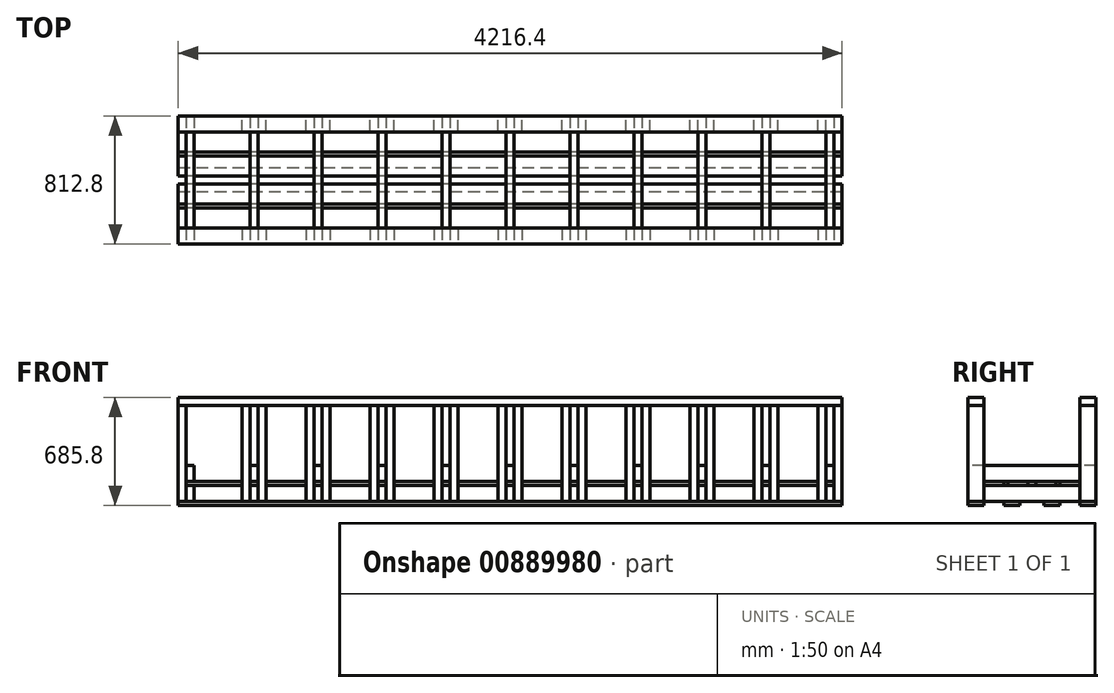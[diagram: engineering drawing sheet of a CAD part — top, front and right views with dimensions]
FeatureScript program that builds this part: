
annotation { "Feature Type Name" : "Feature", "Feature Type Description" : "" }
export const myFeature = defineFeature(function(context is Context, id is Id, definition is map)
    precondition{}
    {
        {
            var Q0;
            Q0=qCreatedBy(makeId("Front.planeOp"),FACE);
            var sketch = newSketch(context, id + "F0", { "sketchPlane" : qUnion([Q0])});
            skLineSegment(sketch, "E0.bottom", {"start": v(-2057.4, 0) * mm, "end": v(-2006.6, 0) * mm});
            skLineSegment(sketch, "E0.top", {"start": v(-2057.4, -101.6) * mm, "end": v(-2006.6, -101.6) * mm});
            skLineSegment(sketch, "E0.left", {"start": v(-2057.4, 0) * mm, "end": v(-2057.4, -101.6) * mm});
            skLineSegment(sketch, "E0.right", {"start": v(-2006.6, 0) * mm, "end": v(-2006.6, -101.6) * mm});
            skLineSegment(sketch, "E1.bottom", {"start": v(-1651, 0) * mm, "end": v(-1600.2, 0) * mm});
            skLineSegment(sketch, "E1.top", {"start": v(-1651, -101.6) * mm, "end": v(-1600.2, -101.6) * mm});
            skLineSegment(sketch, "E1.left", {"start": v(-1651, 0) * mm, "end": v(-1651, -101.6) * mm});
            skLineSegment(sketch, "E1.right", {"start": v(-1600.2, 0) * mm, "end": v(-1600.2, -101.6) * mm});
            skLineSegment(sketch, "E2.bottom", {"start": v(-1244.6, 0) * mm, "end": v(-1193.8, 0) * mm});
            skLineSegment(sketch, "E2.top", {"start": v(-1244.6, -101.6) * mm, "end": v(-1193.8, -101.6) * mm});
            skLineSegment(sketch, "E2.left", {"start": v(-1244.6, 0) * mm, "end": v(-1244.6, -101.6) * mm});
            skLineSegment(sketch, "E2.right", {"start": v(-1193.8, 0) * mm, "end": v(-1193.8, -101.6) * mm});
            skLineSegment(sketch, "E3.bottom", {"start": v(-838.2, 0) * mm, "end": v(-787.4, 0) * mm});
            skLineSegment(sketch, "E3.top", {"start": v(-838.2, -101.6) * mm, "end": v(-787.4, -101.6) * mm});
            skLineSegment(sketch, "E3.left", {"start": v(-838.2, 0) * mm, "end": v(-838.2, -101.6) * mm});
            skLineSegment(sketch, "E3.right", {"start": v(-787.4, 0) * mm, "end": v(-787.4, -101.6) * mm});
            skLineSegment(sketch, "E4.bottom", {"start": v(-431.8, 0) * mm, "end": v(-381, 0) * mm});
            skLineSegment(sketch, "E4.top", {"start": v(-431.8, -101.6) * mm, "end": v(-381, -101.6) * mm});
            skLineSegment(sketch, "E4.left", {"start": v(-431.8, 0) * mm, "end": v(-431.8, -101.6) * mm});
            skLineSegment(sketch, "E4.right", {"start": v(-381, 0) * mm, "end": v(-381, -101.6) * mm});
            skLineSegment(sketch, "E5.bottom", {"start": v(-25.4, 0) * mm, "end": v(25.4, 0) * mm});
            skLineSegment(sketch, "E5.top", {"start": v(-25.4, -101.6) * mm, "end": v(25.4, -101.6) * mm});
            skLineSegment(sketch, "E5.left", {"start": v(-25.4, 0) * mm, "end": v(-25.4, -101.6) * mm});
            skLineSegment(sketch, "E5.right", {"start": v(25.4, 0) * mm, "end": v(25.4, -101.6) * mm});
            skLineSegment(sketch, "E6", {"start": v(0, 664.62) * mm, "end": v(0, -825.58) * mm, "construction": true});
            skPoint(sketch, "E7", {"position": v(-2108.2, -101.6) * mm});
            skPoint(sketch, "E8", {"position": v(-2032, 0) * mm});
            skPoint(sketch, "E9", {"position": v(-1625.6, 0) * mm});
            skPoint(sketch, "E10", {"position": v(-1219.2, 0) * mm});
            skPoint(sketch, "E11", {"position": v(-812.8, 0) * mm});
            skPoint(sketch, "E12", {"position": v(-406.4, 0) * mm});
            skLineSegment(sketch, "E13.MirrorCS", {"start": v(2057.4, 0) * mm, "end": v(2006.6, 0) * mm});
            skLineSegment(sketch, "E14.MirrorCS", {"start": v(2057.4, -101.6) * mm, "end": v(2006.6, -101.6) * mm});
            skLineSegment(sketch, "E15.MirrorCS", {"start": v(1651, -101.6) * mm, "end": v(1600.2, -101.6) * mm});
            skLineSegment(sketch, "E16.MirrorCS", {"start": v(838.2, -101.6) * mm, "end": v(787.4, -101.6) * mm});
            skLineSegment(sketch, "E17.MirrorCS", {"start": v(1244.6, 0) * mm, "end": v(1193.8, 0) * mm});
            skLineSegment(sketch, "E18.MirrorCS", {"start": v(1651, 0) * mm, "end": v(1600.2, 0) * mm});
            skLineSegment(sketch, "E19.MirrorCS", {"start": v(431.8, 0) * mm, "end": v(381, 0) * mm});
            skLineSegment(sketch, "E20.MirrorCS", {"start": v(431.8, -101.6) * mm, "end": v(381, -101.6) * mm});
            skLineSegment(sketch, "E21.MirrorCS", {"start": v(1244.6, -101.6) * mm, "end": v(1193.8, -101.6) * mm});
            skLineSegment(sketch, "E22.MirrorCS", {"start": v(838.2, 0) * mm, "end": v(787.4, 0) * mm});
            skPoint(sketch, "E23.MirrorP", {"position": v(1625.6, 0) * mm});
            skLineSegment(sketch, "E24.MirrorCS", {"start": v(1193.8, 0) * mm, "end": v(1193.8, -101.6) * mm});
            skLineSegment(sketch, "E25.MirrorCS", {"start": v(838.2, 0) * mm, "end": v(838.2, -101.6) * mm});
            skLineSegment(sketch, "E26.MirrorCS", {"start": v(1244.6, 0) * mm, "end": v(1244.6, -101.6) * mm});
            skPoint(sketch, "E27.MirrorP", {"position": v(406.4, 0) * mm});
            skPoint(sketch, "E28.MirrorP", {"position": v(1219.2, 0) * mm});
            skLineSegment(sketch, "E29.MirrorCS", {"start": v(1600.2, 0) * mm, "end": v(1600.2, -101.6) * mm});
            skLineSegment(sketch, "E30.MirrorCS", {"start": v(1651, 0) * mm, "end": v(1651, -101.6) * mm});
            skLineSegment(sketch, "E31.MirrorCS", {"start": v(2057.4, 0) * mm, "end": v(2057.4, -101.6) * mm});
            skLineSegment(sketch, "E32.MirrorCS", {"start": v(2006.6, 0) * mm, "end": v(2006.6, -101.6) * mm});
            skPoint(sketch, "E33.MirrorP", {"position": v(812.8, 0) * mm});
            skLineSegment(sketch, "E34.MirrorCS", {"start": v(787.4, 0) * mm, "end": v(787.4, -101.6) * mm});
            skLineSegment(sketch, "E35.MirrorCS", {"start": v(381, 0) * mm, "end": v(381, -101.6) * mm});
            skPoint(sketch, "E36.MirrorP", {"position": v(2108.2, -101.6) * mm});
            skPoint(sketch, "E37.MirrorP", {"position": v(2032, 0) * mm});
            skLineSegment(sketch, "E38.MirrorCS", {"start": v(431.8, 0) * mm, "end": v(431.8, -101.6) * mm});
            skSolve(sketch);
        }
        {
            var Q0;
            Q0=qSketchRegion(id+"F0",true);
            extrude(context, id + "F1", {"entities" : qUnion([Q0]), "endBound" : BoundingType.SYMMETRIC, "oppositeDirection" : true, "depth" : 812.8 * mm, "offsetDistance" : 25.4 * mm});
        }
        {
            var Q0;
            Q0=makeQuery(id+"F1.opExtrude","SWEPT_FACE",FACE,{"disambiguationData":[OSD([sQuery(id+"F0.wireOp",EDGE,"E0.left")])]});
            var sketch = newSketch(context, id + "F2", { "sketchPlane" : qUnion([Q0])});
            skLineSegment(sketch, "E39.bottom", {"start": v(-25.4, 0) * mm, "end": v(-152.4, 0) * mm});
            skLineSegment(sketch, "E39.top", {"start": v(-25.4, 25.4) * mm, "end": v(-152.4, 25.4) * mm});
            skLineSegment(sketch, "E39.left", {"start": v(-25.4, 0) * mm, "end": v(-25.4, 25.4) * mm});
            skLineSegment(sketch, "E39.right", {"start": v(-152.4, 0) * mm, "end": v(-152.4, 25.4) * mm});
            skLineSegment(sketch, "E40", {"start": v(0, 367.43) * mm, "end": v(0, -336.71) * mm, "construction": true});
            skPoint(sketch, "E40.endSnap0", {"position": v(0, -101.6) * mm});
            skLineSegment(sketch, "E41.bottom", {"start": v(-304.8, 0) * mm, "end": v(-177.8, 0) * mm});
            skLineSegment(sketch, "E41.top", {"start": v(-304.8, 25.4) * mm, "end": v(-177.8, 25.4) * mm});
            skLineSegment(sketch, "E41.left", {"start": v(-304.8, 0) * mm, "end": v(-304.8, 25.4) * mm});
            skLineSegment(sketch, "E41.right", {"start": v(-177.8, 0) * mm, "end": v(-177.8, 25.4) * mm});
            skLineSegment(sketch, "E42.bottom", {"start": v(-406.4, -101.6) * mm, "end": v(-304.8, -101.6) * mm});
            skLineSegment(sketch, "E42.top", {"start": v(-406.4, -127) * mm, "end": v(-304.8, -127) * mm});
            skLineSegment(sketch, "E42.left", {"start": v(-406.4, -101.6) * mm, "end": v(-406.4, -127) * mm});
            skLineSegment(sketch, "E42.right", {"start": v(-304.8, -101.6) * mm, "end": v(-304.8, -127) * mm});
            skLineSegment(sketch, "E43.MirrorCS", {"start": v(152.4, 0) * mm, "end": v(152.4, 25.4) * mm});
            skLineSegment(sketch, "E44.MirrorCS", {"start": v(304.8, 0) * mm, "end": v(177.8, 0) * mm});
            skLineSegment(sketch, "E45.MirrorCS", {"start": v(304.8, 25.4) * mm, "end": v(177.8, 25.4) * mm});
            skLineSegment(sketch, "E46.MirrorCS", {"start": v(25.4, 0) * mm, "end": v(152.4, 0) * mm});
            skLineSegment(sketch, "E47.MirrorCS", {"start": v(177.8, 0) * mm, "end": v(177.8, 25.4) * mm});
            skLineSegment(sketch, "E48.MirrorCS", {"start": v(406.4, -101.6) * mm, "end": v(406.4, -127) * mm});
            skLineSegment(sketch, "E49.MirrorCS", {"start": v(25.4, 25.4) * mm, "end": v(152.4, 25.4) * mm});
            skLineSegment(sketch, "E50.MirrorCS", {"start": v(304.8, 0) * mm, "end": v(304.8, 25.4) * mm});
            skLineSegment(sketch, "E51.MirrorCS", {"start": v(406.4, -127) * mm, "end": v(304.8, -127) * mm});
            skLineSegment(sketch, "E52.MirrorCS", {"start": v(304.8, -101.6) * mm, "end": v(304.8, -127) * mm});
            skLineSegment(sketch, "E53.MirrorCS", {"start": v(406.4, -101.6) * mm, "end": v(304.8, -101.6) * mm});
            skLineSegment(sketch, "E54.MirrorCS", {"start": v(25.4, 0) * mm, "end": v(25.4, 25.4) * mm});
            skLineSegment(sketch, "E55.bottom", {"start": v(-177.8, -101.6) * mm, "end": v(-76.2, -101.6) * mm});
            skLineSegment(sketch, "E55.top", {"start": v(-177.8, -127) * mm, "end": v(-76.2, -127) * mm});
            skLineSegment(sketch, "E55.left", {"start": v(-177.8, -101.6) * mm, "end": v(-177.8, -127) * mm});
            skLineSegment(sketch, "E55.right", {"start": v(-76.2, -101.6) * mm, "end": v(-76.2, -127) * mm});
            skLineSegment(sketch, "E56.MirrorCS", {"start": v(177.8, -101.6) * mm, "end": v(76.2, -101.6) * mm});
            skLineSegment(sketch, "E57.MirrorCS", {"start": v(76.2, -101.6) * mm, "end": v(76.2, -127) * mm});
            skLineSegment(sketch, "E58.MirrorCS", {"start": v(177.8, -101.6) * mm, "end": v(177.8, -127) * mm});
            skLineSegment(sketch, "E59.MirrorCS", {"start": v(177.8, -127) * mm, "end": v(76.2, -127) * mm});
            skSolve(sketch);
        }
        {
            var Q0;
            Q0=qSketchRegion(id+"F2",true);
            var Q1;
            Q1=makeQuery(id+"F1.opExtrude","SWEPT_FACE",FACE,{"disambiguationData":[OSD([sQuery(id+"F0.wireOp",EDGE,"E31.MirrorCS")])]});
            extrude(context, id + "F3", {"entities" : qUnion([Q0]), "endBound" : BoundingType.UP_TO_SURFACE, "oppositeDirection" : true, "depth" : 25.4 * mm, "endBoundEntityFace" : qUnion([Q1]), "hasOffset" : true, "offsetDistance" : -50.8 * mm, "hasSecondDirection" : true, "secondDirectionOppositeDirection" : false, "secondDirectionDepth" : 50.8 * mm});
        }
        {
            var Q0;
            Q0=makeQuery(id+"F3.opExtrude","SWEPT_FACE",FACE,{"disambiguationData":[OSD([sQuery(id+"F2.wireOp",EDGE,"E48.MirrorCS")])]});
            var sketch = newSketch(context, id + "F4", { "sketchPlane" : qUnion([Q0])});
            skLineSegment(sketch, "E60.0", {"start": v(-2057.4, 0) * mm, "end": v(-2057.4, -101.6) * mm});
            skLineSegment(sketch, "E61.0", {"start": v(-2006.6, 0) * mm, "end": v(-2006.6, -101.6) * mm});
            skLineSegment(sketch, "E62.0", {"start": v(-1651, 0) * mm, "end": v(-1651, -101.6) * mm});
            skLineSegment(sketch, "E63.0", {"start": v(-1600.2, 0) * mm, "end": v(-1600.2, -101.6) * mm});
            skLineSegment(sketch, "E64.0", {"start": v(-1244.6, 0) * mm, "end": v(-1244.6, -101.6) * mm});
            skLineSegment(sketch, "E65.0", {"start": v(-1193.8, 0) * mm, "end": v(-1193.8, -101.6) * mm});
            skLineSegment(sketch, "E66.0", {"start": v(-838.2, 0) * mm, "end": v(-838.2, -101.6) * mm});
            skLineSegment(sketch, "E67.0", {"start": v(-787.4, 0) * mm, "end": v(-787.4, -101.6) * mm});
            skLineSegment(sketch, "E68.0", {"start": v(-431.8, 0) * mm, "end": v(-431.8, -101.6) * mm});
            skLineSegment(sketch, "E69.0", {"start": v(-381, 0) * mm, "end": v(-381, -101.6) * mm});
            skLineSegment(sketch, "E70.0", {"start": v(-25.4, 0) * mm, "end": v(-25.4, -101.6) * mm});
            skLineSegment(sketch, "E71.0", {"start": v(25.4, 0) * mm, "end": v(25.4, -101.6) * mm});
            skLineSegment(sketch, "E72.0", {"start": v(381, 0) * mm, "end": v(381, -101.6) * mm});
            skLineSegment(sketch, "E73.0", {"start": v(431.8, 0) * mm, "end": v(431.8, -101.6) * mm});
            skLineSegment(sketch, "E74.0", {"start": v(787.4, 0) * mm, "end": v(787.4, -101.6) * mm});
            skLineSegment(sketch, "E75.0", {"start": v(838.2, 0) * mm, "end": v(838.2, -101.6) * mm});
            skLineSegment(sketch, "E76.0", {"start": v(1193.8, 0) * mm, "end": v(1193.8, -101.6) * mm});
            skLineSegment(sketch, "E77.0", {"start": v(1244.6, 0) * mm, "end": v(1244.6, -101.6) * mm});
            skLineSegment(sketch, "E78.0", {"start": v(1600.2, 0) * mm, "end": v(1600.2, -101.6) * mm});
            skLineSegment(sketch, "E79.0", {"start": v(1651, 0) * mm, "end": v(1651, -101.6) * mm});
            skLineSegment(sketch, "E80.0", {"start": v(2006.6, 0) * mm, "end": v(2006.6, -101.6) * mm});
            skLineSegment(sketch, "E81.0", {"start": v(2057.4, 0) * mm, "end": v(2057.4, -101.6) * mm});
            skLineSegment(sketch, "E82.bottom", {"start": v(-2057.4, 25.4) * mm, "end": v(-2006.6, 25.4) * mm});
            skLineSegment(sketch, "E82.top", {"start": v(-2057.4, 127) * mm, "end": v(-2006.6, 127) * mm});
            skLineSegment(sketch, "E82.left", {"start": v(-2057.4, 25.4) * mm, "end": v(-2057.4, 127) * mm});
            skLineSegment(sketch, "E82.right", {"start": v(-2006.6, 25.4) * mm, "end": v(-2006.6, 127) * mm});
            skLineSegment(sketch, "E83.bottom", {"start": v(-1651, 25.4) * mm, "end": v(-1600.2, 25.4) * mm});
            skLineSegment(sketch, "E83.top", {"start": v(-1651, 127) * mm, "end": v(-1600.2, 127) * mm});
            skLineSegment(sketch, "E83.left", {"start": v(-1651, 25.4) * mm, "end": v(-1651, 127) * mm});
            skLineSegment(sketch, "E83.right", {"start": v(-1600.2, 25.4) * mm, "end": v(-1600.2, 127) * mm});
            skLineSegment(sketch, "E84.bottom", {"start": v(-1244.6, 25.4) * mm, "end": v(-1193.8, 25.4) * mm});
            skLineSegment(sketch, "E84.top", {"start": v(-1244.6, 127) * mm, "end": v(-1193.8, 127) * mm});
            skLineSegment(sketch, "E84.left", {"start": v(-1244.6, 25.4) * mm, "end": v(-1244.6, 127) * mm});
            skLineSegment(sketch, "E84.right", {"start": v(-1193.8, 25.4) * mm, "end": v(-1193.8, 127) * mm});
            skLineSegment(sketch, "E85.bottom", {"start": v(-838.2, 25.4) * mm, "end": v(-787.4, 25.4) * mm});
            skLineSegment(sketch, "E85.top", {"start": v(-838.2, 127) * mm, "end": v(-787.4, 127) * mm});
            skLineSegment(sketch, "E85.left", {"start": v(-838.2, 25.4) * mm, "end": v(-838.2, 127) * mm});
            skLineSegment(sketch, "E85.right", {"start": v(-787.4, 25.4) * mm, "end": v(-787.4, 127) * mm});
            skLineSegment(sketch, "E86.bottom", {"start": v(-431.8, 25.4) * mm, "end": v(-381, 25.4) * mm});
            skLineSegment(sketch, "E86.top", {"start": v(-431.8, 127) * mm, "end": v(-381, 127) * mm});
            skLineSegment(sketch, "E86.left", {"start": v(-431.8, 25.4) * mm, "end": v(-431.8, 127) * mm});
            skLineSegment(sketch, "E86.right", {"start": v(-381, 25.4) * mm, "end": v(-381, 127) * mm});
            skLineSegment(sketch, "E87.bottom", {"start": v(-25.4, 25.4) * mm, "end": v(25.4, 25.4) * mm});
            skLineSegment(sketch, "E87.top", {"start": v(-25.4, 127) * mm, "end": v(25.4, 127) * mm});
            skLineSegment(sketch, "E87.left", {"start": v(-25.4, 25.4) * mm, "end": v(-25.4, 127) * mm});
            skLineSegment(sketch, "E87.right", {"start": v(25.4, 25.4) * mm, "end": v(25.4, 127) * mm});
            skLineSegment(sketch, "E88.bottom", {"start": v(381, 25.4) * mm, "end": v(431.8, 25.4) * mm});
            skLineSegment(sketch, "E88.top", {"start": v(381, 127) * mm, "end": v(431.8, 127) * mm});
            skLineSegment(sketch, "E88.left", {"start": v(381, 25.4) * mm, "end": v(381, 127) * mm});
            skLineSegment(sketch, "E88.right", {"start": v(431.8, 25.4) * mm, "end": v(431.8, 127) * mm});
            skLineSegment(sketch, "E89.bottom", {"start": v(787.4, 25.4) * mm, "end": v(838.2, 25.4) * mm});
            skLineSegment(sketch, "E89.top", {"start": v(787.4, 127) * mm, "end": v(838.2, 127) * mm});
            skLineSegment(sketch, "E89.left", {"start": v(787.4, 25.4) * mm, "end": v(787.4, 127) * mm});
            skLineSegment(sketch, "E89.right", {"start": v(838.2, 25.4) * mm, "end": v(838.2, 127) * mm});
            skLineSegment(sketch, "E90.bottom", {"start": v(1193.8, 25.4) * mm, "end": v(1244.6, 25.4) * mm});
            skLineSegment(sketch, "E90.top", {"start": v(1193.8, 127) * mm, "end": v(1244.6, 127) * mm});
            skLineSegment(sketch, "E90.left", {"start": v(1193.8, 25.4) * mm, "end": v(1193.8, 127) * mm});
            skLineSegment(sketch, "E90.right", {"start": v(1244.6, 25.4) * mm, "end": v(1244.6, 127) * mm});
            skLineSegment(sketch, "E91.bottom", {"start": v(1600.2, 25.4) * mm, "end": v(1651, 25.4) * mm});
            skLineSegment(sketch, "E91.top", {"start": v(1600.2, 127) * mm, "end": v(1651, 127) * mm});
            skLineSegment(sketch, "E91.left", {"start": v(1600.2, 25.4) * mm, "end": v(1600.2, 127) * mm});
            skLineSegment(sketch, "E91.right", {"start": v(1651, 25.4) * mm, "end": v(1651, 127) * mm});
            skLineSegment(sketch, "E92.bottom", {"start": v(2006.6, 25.4) * mm, "end": v(2057.4, 25.4) * mm});
            skLineSegment(sketch, "E92.top", {"start": v(2006.6, 127) * mm, "end": v(2057.4, 127) * mm});
            skLineSegment(sketch, "E92.left", {"start": v(2006.6, 25.4) * mm, "end": v(2006.6, 127) * mm});
            skLineSegment(sketch, "E92.right", {"start": v(2057.4, 25.4) * mm, "end": v(2057.4, 127) * mm});
            skSolve(sketch);
        }
        {
            var Q0;
            Q0=qSketchRegion(id+"F4",true);
            var Q1;
            Q1=makeQuery(id+"F1.opExtrude","CAP_FACE",FACE,{"disambiguationData":[OSD([sQuery(id+"F0.wireOp",EDGE,"E0.bottom"),sQuery(id+"F0.wireOp",EDGE,"E0.top"),sQuery(id+"F0.wireOp",EDGE,"E0.left"),sQuery(id+"F0.wireOp",EDGE,"E0.right")])],"isStart":false});
            extrude(context, id + "F5", {"entities" : qUnion([Q0]), "endBound" : BoundingType.UP_TO_SURFACE, "oppositeDirection" : true, "depth" : 25.4 * mm, "endBoundEntityFace" : qUnion([Q1]), "offsetDistance" : 25.4 * mm});
        }
        {
            var Q0;
            Q0=makeQuery(id+"F3.opExtrude","SWEPT_FACE",FACE,{"disambiguationData":[OSD([sQuery(id+"F2.wireOp",EDGE,"E48.MirrorCS")])]});
            var sketch = newSketch(context, id + "F6", { "sketchPlane" : qUnion([Q0])});
            skLineSegment(sketch, "E93.0", {"start": v(-2057.4, 0) * mm, "end": v(-2057.4, -101.6) * mm});
            skLineSegment(sketch, "E94.0", {"start": v(-2006.6, 0) * mm, "end": v(-2006.6, -101.6) * mm});
            skLineSegment(sketch, "E95.0", {"start": v(-1651, 0) * mm, "end": v(-1651, -101.6) * mm});
            skLineSegment(sketch, "E96.0", {"start": v(-1600.2, 0) * mm, "end": v(-1600.2, -101.6) * mm});
            skLineSegment(sketch, "E97.0", {"start": v(-1193.8, 0) * mm, "end": v(-1193.8, -101.6) * mm});
            skLineSegment(sketch, "E98.0", {"start": v(-1244.6, 0) * mm, "end": v(-1244.6, -101.6) * mm});
            skLineSegment(sketch, "E99.0", {"start": v(-838.2, 0) * mm, "end": v(-838.2, -101.6) * mm});
            skLineSegment(sketch, "E100.0", {"start": v(-787.4, 0) * mm, "end": v(-787.4, -101.6) * mm});
            skLineSegment(sketch, "E101.0", {"start": v(-431.8, 0) * mm, "end": v(-431.8, -101.6) * mm});
            skLineSegment(sketch, "E102.0", {"start": v(-381, 0) * mm, "end": v(-381, -101.6) * mm});
            skLineSegment(sketch, "E103.0", {"start": v(-25.4, 0) * mm, "end": v(-25.4, -101.6) * mm});
            skLineSegment(sketch, "E104.0", {"start": v(25.4, 0) * mm, "end": v(25.4, -101.6) * mm});
            skLineSegment(sketch, "E105.0", {"start": v(381, 0) * mm, "end": v(381, -101.6) * mm});
            skLineSegment(sketch, "E106.0", {"start": v(431.8, 0) * mm, "end": v(431.8, -101.6) * mm});
            skLineSegment(sketch, "E107.0", {"start": v(787.4, 0) * mm, "end": v(787.4, -101.6) * mm});
            skLineSegment(sketch, "E108.0", {"start": v(838.2, 0) * mm, "end": v(838.2, -101.6) * mm});
            skLineSegment(sketch, "E109.0", {"start": v(1193.8, 0) * mm, "end": v(1193.8, -101.6) * mm});
            skLineSegment(sketch, "E110.0", {"start": v(1244.6, 0) * mm, "end": v(1244.6, -101.6) * mm});
            skLineSegment(sketch, "E111.0", {"start": v(1600.2, 0) * mm, "end": v(1600.2, -101.6) * mm});
            skLineSegment(sketch, "E112.0", {"start": v(1651, 0) * mm, "end": v(1651, -101.6) * mm});
            skLineSegment(sketch, "E113.0", {"start": v(2006.6, 0) * mm, "end": v(2006.6, -101.6) * mm});
            skLineSegment(sketch, "E114.0", {"start": v(2057.4, 0) * mm, "end": v(2057.4, -101.6) * mm});
            skLineSegment(sketch, "E115.bottom", {"start": v(-2108.2, -101.6) * mm, "end": v(-2057.4, -101.6) * mm});
            skLineSegment(sketch, "E115.top", {"start": v(-2108.2, 508) * mm, "end": v(-2057.4, 508) * mm});
            skLineSegment(sketch, "E115.left", {"start": v(-2108.2, -101.6) * mm, "end": v(-2108.2, 508) * mm});
            skLineSegment(sketch, "E115.right", {"start": v(-2057.4, -101.6) * mm, "end": v(-2057.4, 508) * mm});
            skLineSegment(sketch, "E116.bottom", {"start": v(-1651, -101.6) * mm, "end": v(-1701.8, -101.6) * mm});
            skLineSegment(sketch, "E116.top", {"start": v(-1651, 508) * mm, "end": v(-1701.8, 508) * mm});
            skLineSegment(sketch, "E116.left", {"start": v(-1651, -101.6) * mm, "end": v(-1651, 508) * mm});
            skLineSegment(sketch, "E116.right", {"start": v(-1701.8, -101.6) * mm, "end": v(-1701.8, 508) * mm});
            skLineSegment(sketch, "E117.bottom", {"start": v(-1600.2, -101.6) * mm, "end": v(-1549.4, -101.6) * mm});
            skLineSegment(sketch, "E117.top", {"start": v(-1600.2, 508) * mm, "end": v(-1549.4, 508) * mm});
            skLineSegment(sketch, "E117.left", {"start": v(-1600.2, -101.6) * mm, "end": v(-1600.2, 508) * mm});
            skLineSegment(sketch, "E117.right", {"start": v(-1549.4, -101.6) * mm, "end": v(-1549.4, 508) * mm});
            skLineSegment(sketch, "E118.bottom", {"start": v(-1244.6, -101.6) * mm, "end": v(-1295.4, -101.6) * mm});
            skLineSegment(sketch, "E118.top", {"start": v(-1244.6, 508) * mm, "end": v(-1295.4, 508) * mm});
            skLineSegment(sketch, "E118.left", {"start": v(-1244.6, -101.6) * mm, "end": v(-1244.6, 508) * mm});
            skLineSegment(sketch, "E118.right", {"start": v(-1295.4, -101.6) * mm, "end": v(-1295.4, 508) * mm});
            skLineSegment(sketch, "E119.bottom", {"start": v(-1193.8, -101.6) * mm, "end": v(-1143, -101.6) * mm});
            skLineSegment(sketch, "E119.top", {"start": v(-1193.8, 508) * mm, "end": v(-1143, 508) * mm});
            skLineSegment(sketch, "E119.left", {"start": v(-1193.8, -101.6) * mm, "end": v(-1193.8, 508) * mm});
            skLineSegment(sketch, "E119.right", {"start": v(-1143, -101.6) * mm, "end": v(-1143, 508) * mm});
            skLineSegment(sketch, "E120.bottom", {"start": v(-838.2, -101.6) * mm, "end": v(-889, -101.6) * mm});
            skLineSegment(sketch, "E120.top", {"start": v(-838.2, 508) * mm, "end": v(-889, 508) * mm});
            skLineSegment(sketch, "E120.left", {"start": v(-838.2, -101.6) * mm, "end": v(-838.2, 508) * mm});
            skLineSegment(sketch, "E120.right", {"start": v(-889, -101.6) * mm, "end": v(-889, 508) * mm});
            skLineSegment(sketch, "E121.bottom", {"start": v(-787.4, -101.6) * mm, "end": v(-736.6, -101.6) * mm});
            skLineSegment(sketch, "E121.top", {"start": v(-787.4, 508) * mm, "end": v(-736.6, 508) * mm});
            skLineSegment(sketch, "E121.left", {"start": v(-787.4, -101.6) * mm, "end": v(-787.4, 508) * mm});
            skLineSegment(sketch, "E121.right", {"start": v(-736.6, -101.6) * mm, "end": v(-736.6, 508) * mm});
            skLineSegment(sketch, "E122.bottom", {"start": v(-431.8, -101.6) * mm, "end": v(-482.6, -101.6) * mm});
            skLineSegment(sketch, "E122.top", {"start": v(-431.8, 508) * mm, "end": v(-482.6, 508) * mm});
            skLineSegment(sketch, "E122.left", {"start": v(-431.8, -101.6) * mm, "end": v(-431.8, 508) * mm});
            skLineSegment(sketch, "E122.right", {"start": v(-482.6, -101.6) * mm, "end": v(-482.6, 508) * mm});
            skLineSegment(sketch, "E123.bottom", {"start": v(-381, -101.6) * mm, "end": v(-330.2, -101.6) * mm});
            skLineSegment(sketch, "E123.top", {"start": v(-381, 508) * mm, "end": v(-330.2, 508) * mm});
            skLineSegment(sketch, "E123.left", {"start": v(-381, -101.6) * mm, "end": v(-381, 508) * mm});
            skLineSegment(sketch, "E123.right", {"start": v(-330.2, -101.6) * mm, "end": v(-330.2, 508) * mm});
            skLineSegment(sketch, "E124.bottom", {"start": v(-25.4, -101.6) * mm, "end": v(-76.2, -101.6) * mm});
            skLineSegment(sketch, "E124.top", {"start": v(-25.4, 508) * mm, "end": v(-76.2, 508) * mm});
            skLineSegment(sketch, "E124.left", {"start": v(-25.4, -101.6) * mm, "end": v(-25.4, 508) * mm});
            skLineSegment(sketch, "E124.right", {"start": v(-76.2, -101.6) * mm, "end": v(-76.2, 508) * mm});
            skLineSegment(sketch, "E125.bottom", {"start": v(25.4, -101.6) * mm, "end": v(76.2, -101.6) * mm});
            skLineSegment(sketch, "E125.top", {"start": v(25.4, 508) * mm, "end": v(76.2, 508) * mm});
            skLineSegment(sketch, "E125.left", {"start": v(25.4, -101.6) * mm, "end": v(25.4, 508) * mm});
            skLineSegment(sketch, "E125.right", {"start": v(76.2, -101.6) * mm, "end": v(76.2, 508) * mm});
            skLineSegment(sketch, "E126.bottom", {"start": v(381, -101.6) * mm, "end": v(330.2, -101.6) * mm});
            skLineSegment(sketch, "E126.top", {"start": v(381, 508) * mm, "end": v(330.2, 508) * mm});
            skLineSegment(sketch, "E126.left", {"start": v(381, -101.6) * mm, "end": v(381, 508) * mm});
            skLineSegment(sketch, "E126.right", {"start": v(330.2, -101.6) * mm, "end": v(330.2, 508) * mm});
            skLineSegment(sketch, "E127.bottom", {"start": v(431.8, -101.6) * mm, "end": v(482.6, -101.6) * mm});
            skLineSegment(sketch, "E127.top", {"start": v(431.8, 508) * mm, "end": v(482.6, 508) * mm});
            skLineSegment(sketch, "E127.left", {"start": v(431.8, -101.6) * mm, "end": v(431.8, 508) * mm});
            skLineSegment(sketch, "E127.right", {"start": v(482.6, -101.6) * mm, "end": v(482.6, 508) * mm});
            skLineSegment(sketch, "E128.bottom", {"start": v(787.4, -101.6) * mm, "end": v(736.6, -101.6) * mm});
            skLineSegment(sketch, "E128.top", {"start": v(787.4, 508) * mm, "end": v(736.6, 508) * mm});
            skLineSegment(sketch, "E128.left", {"start": v(787.4, -101.6) * mm, "end": v(787.4, 508) * mm});
            skLineSegment(sketch, "E128.right", {"start": v(736.6, -101.6) * mm, "end": v(736.6, 508) * mm});
            skLineSegment(sketch, "E129.bottom", {"start": v(838.2, -101.6) * mm, "end": v(889, -101.6) * mm});
            skLineSegment(sketch, "E129.top", {"start": v(838.2, 508) * mm, "end": v(889, 508) * mm});
            skLineSegment(sketch, "E129.left", {"start": v(838.2, -101.6) * mm, "end": v(838.2, 508) * mm});
            skLineSegment(sketch, "E129.right", {"start": v(889, -101.6) * mm, "end": v(889, 508) * mm});
            skLineSegment(sketch, "E130.bottom", {"start": v(1193.8, -101.6) * mm, "end": v(1143, -101.6) * mm});
            skLineSegment(sketch, "E130.top", {"start": v(1193.8, 508) * mm, "end": v(1143, 508) * mm});
            skLineSegment(sketch, "E130.left", {"start": v(1193.8, -101.6) * mm, "end": v(1193.8, 508) * mm});
            skLineSegment(sketch, "E130.right", {"start": v(1143, -101.6) * mm, "end": v(1143, 508) * mm});
            skLineSegment(sketch, "E131.bottom", {"start": v(1244.6, -101.6) * mm, "end": v(1295.4, -101.6) * mm});
            skLineSegment(sketch, "E131.top", {"start": v(1244.6, 508) * mm, "end": v(1295.4, 508) * mm});
            skLineSegment(sketch, "E131.left", {"start": v(1244.6, -101.6) * mm, "end": v(1244.6, 508) * mm});
            skLineSegment(sketch, "E131.right", {"start": v(1295.4, -101.6) * mm, "end": v(1295.4, 508) * mm});
            skLineSegment(sketch, "E132.bottom", {"start": v(1600.2, -101.6) * mm, "end": v(1549.4, -101.6) * mm});
            skLineSegment(sketch, "E132.top", {"start": v(1600.2, 508) * mm, "end": v(1549.4, 508) * mm});
            skLineSegment(sketch, "E132.left", {"start": v(1600.2, -101.6) * mm, "end": v(1600.2, 508) * mm});
            skLineSegment(sketch, "E132.right", {"start": v(1549.4, -101.6) * mm, "end": v(1549.4, 508) * mm});
            skLineSegment(sketch, "E133.bottom", {"start": v(1651, -101.6) * mm, "end": v(1701.8, -101.6) * mm});
            skLineSegment(sketch, "E133.top", {"start": v(1651, 508) * mm, "end": v(1701.8, 508) * mm});
            skLineSegment(sketch, "E133.left", {"start": v(1651, -101.6) * mm, "end": v(1651, 508) * mm});
            skLineSegment(sketch, "E133.right", {"start": v(1701.8, -101.6) * mm, "end": v(1701.8, 508) * mm});
            skLineSegment(sketch, "E134.bottom", {"start": v(2006.6, -101.6) * mm, "end": v(1955.8, -101.6) * mm});
            skLineSegment(sketch, "E134.top", {"start": v(2006.6, 508) * mm, "end": v(1955.8, 508) * mm});
            skLineSegment(sketch, "E134.left", {"start": v(2006.6, -101.6) * mm, "end": v(2006.6, 508) * mm});
            skLineSegment(sketch, "E134.right", {"start": v(1955.8, -101.6) * mm, "end": v(1955.8, 508) * mm});
            skLineSegment(sketch, "E135.bottom", {"start": v(2057.4, -101.6) * mm, "end": v(2108.2, -101.6) * mm});
            skLineSegment(sketch, "E135.top", {"start": v(2057.4, 508) * mm, "end": v(2108.2, 508) * mm});
            skLineSegment(sketch, "E135.left", {"start": v(2057.4, -101.6) * mm, "end": v(2057.4, 508) * mm});
            skLineSegment(sketch, "E135.right", {"start": v(2108.2, -101.6) * mm, "end": v(2108.2, 508) * mm});
            skSolve(sketch);
        }
        {
            var Q0;
            Q0=qSketchRegion(id+"F6",true);
            extrude(context, id + "F7", {"entities" : qUnion([Q0]), "oppositeDirection" : true, "depth" : 101.6 * mm, "offsetDistance" : 25.4 * mm});
        }
        {
            var Q0;
            Q0=makeQuery(id+"F1.opExtrude","CAP_FACE",FACE,{"disambiguationData":[OSD([sQuery(id+"F0.wireOp",EDGE,"E0.bottom"),sQuery(id+"F0.wireOp",EDGE,"E0.top"),sQuery(id+"F0.wireOp",EDGE,"E0.left"),sQuery(id+"F0.wireOp",EDGE,"E0.right")])],"isStart":false});
            var sketch = newSketch(context, id + "F8", { "sketchPlane" : qUnion([Q0])});
            skLineSegment(sketch, "E136.0", {"start": v(1600.2, -101.6) * mm, "end": v(1549.4, -101.6) * mm});
            skLineSegment(sketch, "E136.1", {"start": v(-482.6, -101.6) * mm, "end": v(-482.6, 508) * mm});
            skLineSegment(sketch, "E136.2", {"start": v(1143, -101.6) * mm, "end": v(1143, 508) * mm});
            skLineSegment(sketch, "E136.3", {"start": v(1651, -101.6) * mm, "end": v(1701.8, -101.6) * mm});
            skLineSegment(sketch, "E136.4", {"start": v(838.2, 508) * mm, "end": v(889, 508) * mm});
            skLineSegment(sketch, "E136.5", {"start": v(-1600.2, 508) * mm, "end": v(-1549.4, 508) * mm});
            skLineSegment(sketch, "E136.6", {"start": v(-787.4, 508) * mm, "end": v(-736.6, 508) * mm});
            skLineSegment(sketch, "E136.7", {"start": v(1651, 508) * mm, "end": v(1701.8, 508) * mm});
            skLineSegment(sketch, "E136.8", {"start": v(838.2, -101.6) * mm, "end": v(889, -101.6) * mm});
            skLineSegment(sketch, "E136.9", {"start": v(-1295.4, -101.6) * mm, "end": v(-1295.4, 508) * mm});
            skLineSegment(sketch, "E136.10", {"start": v(2057.4, -101.6) * mm, "end": v(2057.4, 508) * mm});
            skLineSegment(sketch, "E136.11", {"start": v(-431.8, -101.6) * mm, "end": v(-431.8, 508) * mm});
            skLineSegment(sketch, "E136.12", {"start": v(25.4, 508) * mm, "end": v(76.2, 508) * mm});
            skLineSegment(sketch, "E136.13", {"start": v(330.2, -101.6) * mm, "end": v(330.2, 508) * mm});
            skLineSegment(sketch, "E136.14", {"start": v(-1244.6, -101.6) * mm, "end": v(-1244.6, 508) * mm});
            skLineSegment(sketch, "E136.15", {"start": v(-2057.4, 508) * mm, "end": v(-2108.2, 508) * mm});
            skLineSegment(sketch, "E136.16", {"start": v(838.2, -101.6) * mm, "end": v(838.2, 508) * mm});
            skLineSegment(sketch, "E136.17", {"start": v(-2108.2, -101.6) * mm, "end": v(-2108.2, 508) * mm});
            skLineSegment(sketch, "E136.18", {"start": v(-1244.6, 508) * mm, "end": v(-1295.4, 508) * mm});
            skLineSegment(sketch, "E136.19", {"start": v(1193.8, 508) * mm, "end": v(1143, 508) * mm});
            skLineSegment(sketch, "E136.20", {"start": v(381, 508) * mm, "end": v(330.2, 508) * mm});
            skLineSegment(sketch, "E136.21", {"start": v(-431.8, 508) * mm, "end": v(-482.6, 508) * mm});
            skLineSegment(sketch, "E136.22", {"start": v(2108.2, 508) * mm, "end": v(2057.4, 508) * mm});
            skLineSegment(sketch, "E136.23", {"start": v(25.4, -101.6) * mm, "end": v(76.2, -101.6) * mm});
            skLineSegment(sketch, "E136.24", {"start": v(-787.4, -101.6) * mm, "end": v(-736.6, -101.6) * mm});
            skLineSegment(sketch, "E136.25", {"start": v(-1600.2, -101.6) * mm, "end": v(-1549.4, -101.6) * mm});
            skLineSegment(sketch, "E136.26", {"start": v(-2057.4, -101.6) * mm, "end": v(-2057.4, 508) * mm});
            skLineSegment(sketch, "E136.27", {"start": v(2108.2, -101.6) * mm, "end": v(2108.2, 508) * mm});
            skLineSegment(sketch, "E136.28", {"start": v(381, -101.6) * mm, "end": v(381, 508) * mm});
            skLineSegment(sketch, "E136.29", {"start": v(1193.8, -101.6) * mm, "end": v(1193.8, 508) * mm});
            skLineSegment(sketch, "E136.30", {"start": v(889, -101.6) * mm, "end": v(889, 508) * mm});
            skLineSegment(sketch, "E136.31", {"start": v(1701.8, -101.6) * mm, "end": v(1701.8, 508) * mm});
            skLineSegment(sketch, "E136.32", {"start": v(-1651, -101.6) * mm, "end": v(-1701.8, -101.6) * mm});
            skLineSegment(sketch, "E136.33", {"start": v(-1549.4, -101.6) * mm, "end": v(-1549.4, 508) * mm});
            skLineSegment(sketch, "E136.34", {"start": v(-736.6, -101.6) * mm, "end": v(-736.6, 508) * mm});
            skLineSegment(sketch, "E136.35", {"start": v(1651, -101.6) * mm, "end": v(1651, 508) * mm});
            skLineSegment(sketch, "E136.36", {"start": v(-1600.2, -101.6) * mm, "end": v(-1600.2, 508) * mm});
            skLineSegment(sketch, "E136.37", {"start": v(-787.4, -101.6) * mm, "end": v(-787.4, 508) * mm});
            skLineSegment(sketch, "E136.38", {"start": v(25.4, -101.6) * mm, "end": v(25.4, 508) * mm});
            skLineSegment(sketch, "E136.39", {"start": v(787.4, -101.6) * mm, "end": v(736.6, -101.6) * mm});
            skLineSegment(sketch, "E136.40", {"start": v(76.2, -101.6) * mm, "end": v(76.2, 508) * mm});
            skLineSegment(sketch, "E136.41", {"start": v(-838.2, -101.6) * mm, "end": v(-889, -101.6) * mm});
            skLineSegment(sketch, "E136.42", {"start": v(-25.4, -101.6) * mm, "end": v(-76.2, -101.6) * mm});
            skLineSegment(sketch, "E136.43", {"start": v(787.4, 508) * mm, "end": v(736.6, 508) * mm});
            skLineSegment(sketch, "E136.44", {"start": v(1600.2, 508) * mm, "end": v(1549.4, 508) * mm});
            skLineSegment(sketch, "E136.45", {"start": v(-1651, 508) * mm, "end": v(-1701.8, 508) * mm});
            skLineSegment(sketch, "E136.46", {"start": v(-838.2, 508) * mm, "end": v(-889, 508) * mm});
            skLineSegment(sketch, "E136.47", {"start": v(-25.4, 508) * mm, "end": v(-76.2, 508) * mm});
            skLineSegment(sketch, "E136.48", {"start": v(787.4, -101.6) * mm, "end": v(787.4, 508) * mm});
            skLineSegment(sketch, "E136.49", {"start": v(1600.2, -101.6) * mm, "end": v(1600.2, 508) * mm});
            skLineSegment(sketch, "E136.50", {"start": v(-1193.8, 0) * mm, "end": v(-1193.8, -101.6) * mm});
            skLineSegment(sketch, "E136.51", {"start": v(-1651, -101.6) * mm, "end": v(-1651, 508) * mm});
            skLineSegment(sketch, "E136.52", {"start": v(-838.2, -101.6) * mm, "end": v(-838.2, 508) * mm});
            skLineSegment(sketch, "E136.53", {"start": v(-25.4, -101.6) * mm, "end": v(-25.4, 508) * mm});
            skLineSegment(sketch, "E136.54", {"start": v(736.6, -101.6) * mm, "end": v(736.6, 508) * mm});
            skLineSegment(sketch, "E136.55", {"start": v(1549.4, -101.6) * mm, "end": v(1549.4, 508) * mm});
            skLineSegment(sketch, "E136.56", {"start": v(-1244.6, 0) * mm, "end": v(-1244.6, -101.6) * mm});
            skLineSegment(sketch, "E136.57", {"start": v(-1701.8, -101.6) * mm, "end": v(-1701.8, 508) * mm});
            skLineSegment(sketch, "E136.58", {"start": v(-889, -101.6) * mm, "end": v(-889, 508) * mm});
            skLineSegment(sketch, "E136.59", {"start": v(-76.2, -101.6) * mm, "end": v(-76.2, 508) * mm});
            skLineSegment(sketch, "E136.60", {"start": v(-2006.6, -101.6) * mm, "end": v(-1955.8, -101.6) * mm});
            skLineSegment(sketch, "E136.61", {"start": v(-1193.8, -101.6) * mm, "end": v(-1143, -101.6) * mm});
            skLineSegment(sketch, "E136.62", {"start": v(-381, -101.6) * mm, "end": v(-330.2, -101.6) * mm});
            skLineSegment(sketch, "E136.63", {"start": v(431.8, -101.6) * mm, "end": v(482.6, -101.6) * mm});
            skLineSegment(sketch, "E136.64", {"start": v(1244.6, -101.6) * mm, "end": v(1295.4, -101.6) * mm});
            skLineSegment(sketch, "E136.65", {"start": v(-1600.2, 0) * mm, "end": v(-1600.2, -101.6) * mm});
            skLineSegment(sketch, "E136.66", {"start": v(431.8, 508) * mm, "end": v(482.6, 508) * mm});
            skLineSegment(sketch, "E136.67", {"start": v(1244.6, 508) * mm, "end": v(1295.4, 508) * mm});
            skLineSegment(sketch, "E136.68", {"start": v(-1651, 0) * mm, "end": v(-1651, -101.6) * mm});
            skLineSegment(sketch, "E136.69", {"start": v(-2006.6, 508) * mm, "end": v(-1955.8, 508) * mm});
            skLineSegment(sketch, "E136.70", {"start": v(-1193.8, 508) * mm, "end": v(-1143, 508) * mm});
            skLineSegment(sketch, "E136.71", {"start": v(-381, 508) * mm, "end": v(-330.2, 508) * mm});
            skLineSegment(sketch, "E136.72", {"start": v(431.8, -101.6) * mm, "end": v(431.8, 508) * mm});
            skLineSegment(sketch, "E136.73", {"start": v(1244.6, -101.6) * mm, "end": v(1244.6, 508) * mm});
            skLineSegment(sketch, "E136.74", {"start": v(-2006.6, 0) * mm, "end": v(-2006.6, -101.6) * mm});
            skLineSegment(sketch, "E136.75", {"start": v(-2006.6, -101.6) * mm, "end": v(-2006.6, 508) * mm});
            skLineSegment(sketch, "E136.76", {"start": v(-1193.8, -101.6) * mm, "end": v(-1193.8, 508) * mm});
            skLineSegment(sketch, "E136.77", {"start": v(-381, -101.6) * mm, "end": v(-381, 508) * mm});
            skLineSegment(sketch, "E136.78", {"start": v(482.6, -101.6) * mm, "end": v(482.6, 508) * mm});
            skLineSegment(sketch, "E136.79", {"start": v(1295.4, -101.6) * mm, "end": v(1295.4, 508) * mm});
            skLineSegment(sketch, "E136.80", {"start": v(-2057.4, 0) * mm, "end": v(-2057.4, -101.6) * mm});
            skLineSegment(sketch, "E136.81", {"start": v(-1955.8, -101.6) * mm, "end": v(-1955.8, 508) * mm});
            skLineSegment(sketch, "E136.82", {"start": v(-1143, -101.6) * mm, "end": v(-1143, 508) * mm});
            skLineSegment(sketch, "E136.83", {"start": v(-330.2, -101.6) * mm, "end": v(-330.2, 508) * mm});
            skLineSegment(sketch, "E136.84", {"start": v(381, -101.6) * mm, "end": v(330.2, -101.6) * mm});
            skLineSegment(sketch, "E136.85", {"start": v(1193.8, -101.6) * mm, "end": v(1143, -101.6) * mm});
            skLineSegment(sketch, "E136.86", {"start": v(2108.2, -101.6) * mm, "end": v(2057.4, -101.6) * mm});
            skLineSegment(sketch, "E136.87", {"start": v(-2057.4, -101.6) * mm, "end": v(-2108.2, -101.6) * mm});
            skLineSegment(sketch, "E136.88", {"start": v(-1244.6, -101.6) * mm, "end": v(-1295.4, -101.6) * mm});
            skLineSegment(sketch, "E136.89", {"start": v(-431.8, -101.6) * mm, "end": v(-482.6, -101.6) * mm});
            skLineSegment(sketch, "E136.90", {"start": v(-431.8, 0) * mm, "end": v(-431.8, -101.6) * mm});
            skLineSegment(sketch, "E136.91", {"start": v(-787.4, 0) * mm, "end": v(-787.4, -101.6) * mm});
            skLineSegment(sketch, "E136.92", {"start": v(-838.2, 0) * mm, "end": v(-838.2, -101.6) * mm});
            skLineSegment(sketch, "E136.93", {"start": v(2057.4, 0) * mm, "end": v(2057.4, -101.6) * mm});
            skLineSegment(sketch, "E136.94", {"start": v(2006.6, 0) * mm, "end": v(2006.6, -101.6) * mm});
            skLineSegment(sketch, "E136.95", {"start": v(1651, 0) * mm, "end": v(1651, -101.6) * mm});
            skLineSegment(sketch, "E136.96", {"start": v(1600.2, 0) * mm, "end": v(1600.2, -101.6) * mm});
            skLineSegment(sketch, "E136.97", {"start": v(1193.8, 0) * mm, "end": v(1193.8, -101.6) * mm});
            skLineSegment(sketch, "E136.98", {"start": v(1244.6, 0) * mm, "end": v(1244.6, -101.6) * mm});
            skLineSegment(sketch, "E136.99", {"start": v(838.2, 0) * mm, "end": v(838.2, -101.6) * mm});
            skLineSegment(sketch, "E136.100", {"start": v(787.4, 0) * mm, "end": v(787.4, -101.6) * mm});
            skLineSegment(sketch, "E136.101", {"start": v(431.8, 0) * mm, "end": v(431.8, -101.6) * mm});
            skLineSegment(sketch, "E136.102", {"start": v(381, 0) * mm, "end": v(381, -101.6) * mm});
            skLineSegment(sketch, "E136.103", {"start": v(25.4, 0) * mm, "end": v(25.4, -101.6) * mm});
            skLineSegment(sketch, "E136.104", {"start": v(-25.4, 0) * mm, "end": v(-25.4, -101.6) * mm});
            skLineSegment(sketch, "E136.105", {"start": v(-381, 0) * mm, "end": v(-381, -101.6) * mm});
            skSolve(sketch);
        }
        {
            var Q0;
            Q0=qSketchRegion(id+"F8",true);
            extrude(context, id + "F9", {"entities" : qUnion([Q0]), "oppositeDirection" : true, "depth" : 101.6 * mm, "offsetDistance" : 25.4 * mm});
        }
        {
            var Q0;
            Q0=makeQuery(id+"F7.opExtrude","SWEPT_FACE",FACE,{"disambiguationData":[OSD([sQuery(id+"F6.wireOp",EDGE,"E135.right")])]});
            var sketch = newSketch(context, id + "F10", { "sketchPlane" : qUnion([Q0])});
            skLineSegment(sketch, "E137.0", {"start": v(406.4, -101.6) * mm, "end": v(406.4, 508) * mm});
            skLineSegment(sketch, "E138.0", {"start": v(304.8, -101.6) * mm, "end": v(304.8, 508) * mm});
            skLineSegment(sketch, "E139.0", {"start": v(304.8, 508) * mm, "end": v(406.4, 508) * mm});
            skLineSegment(sketch, "E140.bottom", {"start": v(-406.4, 508) * mm, "end": v(-304.8, 508) * mm});
            skLineSegment(sketch, "E140.top", {"start": v(-406.4, 558.8) * mm, "end": v(-304.8, 558.8) * mm});
            skLineSegment(sketch, "E140.left", {"start": v(-406.4, 508) * mm, "end": v(-406.4, 558.8) * mm});
            skLineSegment(sketch, "E140.right", {"start": v(-304.8, 508) * mm, "end": v(-304.8, 558.8) * mm});
            skLineSegment(sketch, "E141.top", {"start": v(304.8, 558.8) * mm, "end": v(406.4, 558.8) * mm});
            skLineSegment(sketch, "E141.left", {"start": v(304.8, 508) * mm, "end": v(304.8, 558.8) * mm});
            skLineSegment(sketch, "E141.right", {"start": v(406.4, 508) * mm, "end": v(406.4, 558.8) * mm});
            skSolve(sketch);
        }
        {
            var Q0;
            Q0=makeQuery(id+"F10.imprint","IMPRINT",FACE,{"disambiguationData":[TD([[makeQuery(id+"F10.imprint","IMPRINT",EDGE,{"derivedFrom":sQuery(id+"F10.wireOp",EDGE,"E140.bottom")}),-1.0]])]});
            var Q1;
            Q1=makeQuery(id+"F10.imprint","IMPRINT",FACE,{"disambiguationData":[TD([[makeQuery(id+"F10.imprint","IMPRINT",EDGE,{"derivedFrom":sQuery(id+"F10.wireOp",EDGE,"E139.0")}),1.0]])]});
            var Q2;
            Q2=makeQuery(id+"F9.opExtrude","SWEPT_FACE",FACE,{"disambiguationData":[OSD([sQuery(id+"F8.wireOp",EDGE,"E136.27")])]});
            extrude(context, id + "F11", {"entities" : qUnion([Q0, Q1]), "endBound" : BoundingType.UP_TO_SURFACE, "oppositeDirection" : true, "depth" : 25.4 * mm, "endBoundEntityFace" : qUnion([Q2]), "offsetDistance" : 25.4 * mm});
        }
    });
